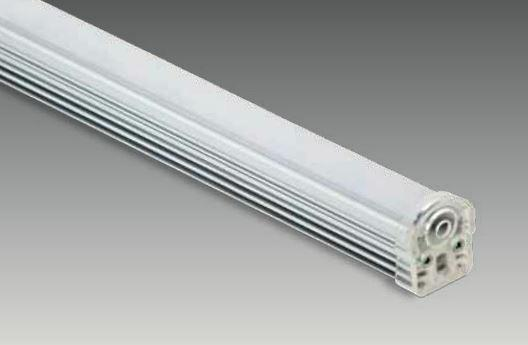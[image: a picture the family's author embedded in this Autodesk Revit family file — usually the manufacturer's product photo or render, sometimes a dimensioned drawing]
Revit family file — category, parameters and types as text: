
# Revit family: SD 1495 CVK
name_source: partatom
category: Lighting Fixtures
revit_build: Autodesk Revit 2017 (Build: 20160225_1515(x64)
units: mm (PartAtom-declared; Revit-internal decimal feet)

## family parameters
Cut with Voids When Loaded = No
Host = Face
Light Source = Yes
Part Type = Normal
Room Calculation Point = No
Round Connector Dimension = Use Diameter
Shared = No

## types (2) — shared parameters
Apparent Load = 36 VA
Color Filter = 16777215
Default Elevation = 1219 mm
Dimming Lamp Color Temperature Shift = <None>
Emit Shape Visible in Rendering = Yes
Emit from Rectangle Length = 15 mm  [stored 0.0492126 ft]
Emit from Rectangle Width = 1490 mm  [stored 4.88845 ft]
Light Source Symbol Size = 610 mm
Manufacturer = ARLIGHT
Type Image = SD 1495 CVK.JPG
Wattage Comments = 36

## type names (no varying parameters)
- SDCVK.1495.36.30
- SDCVK.1495.36.40

note: [stored X ft] marks values corroborated as IEEE doubles in the binary element streams (Revit-internal decimal feet)

## geometry (parser evidence)
native form markers: Sweep x3
no freeform markers — native parametric forms only
